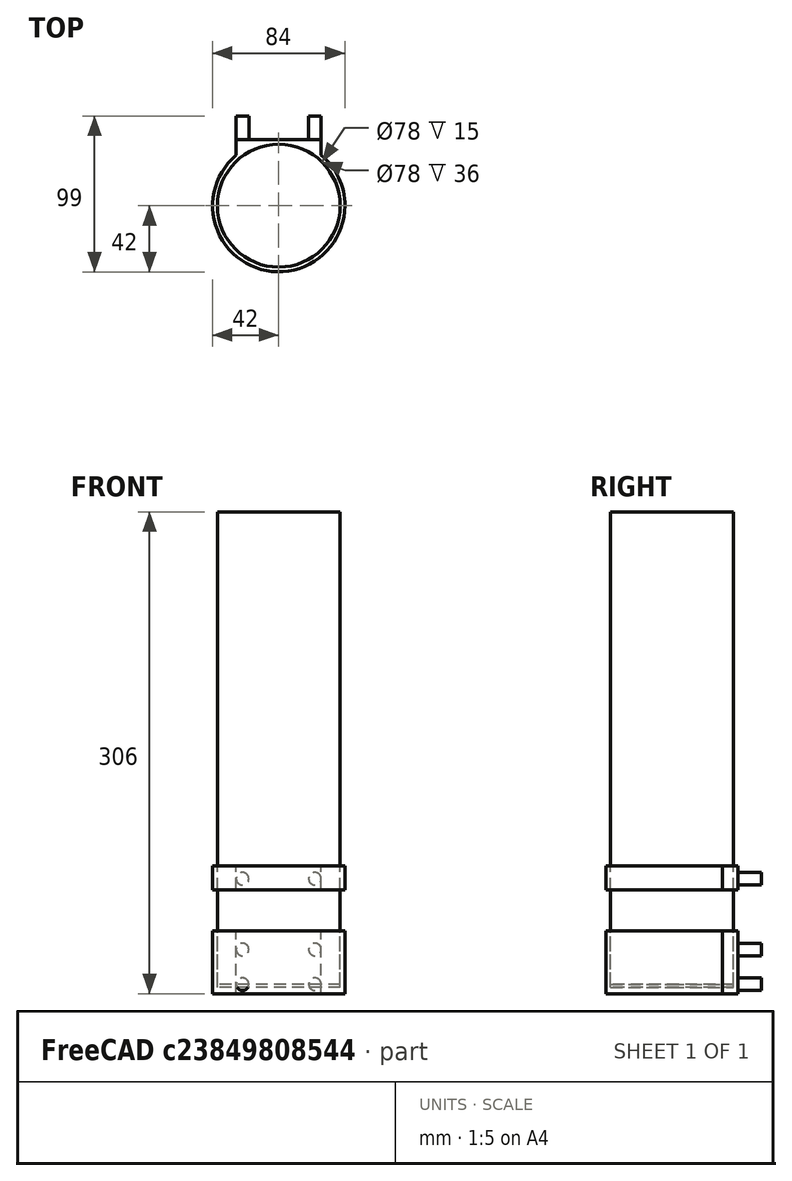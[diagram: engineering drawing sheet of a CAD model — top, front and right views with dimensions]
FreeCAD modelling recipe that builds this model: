
FCSTD DOCUMENT  (FreeCAD 0.15R4671 (Git))
Label: Holder_V10
License: All rights reserved
LicenseURL: http://en.wikipedia.org/wiki/All_rights_reserved
objects: Part::Cylinder×11, Part::Box×2, Part::MultiFuse×2, Part::Cut×2
note: 17 computed .brp shape members not serialized (recipe doc carries the construction recipe); baked Part::Feature solids carry a one-line shape summary decoded from their .brp

FEATURE [Part::Cylinder] Cylinder  label="Pin1"
  Angle = 360
  Height = 15
  Placement = pos=(0,5,0) rot=(1,0,0;1.5708rad)
  Radius = 4
FEATURE [Part::Cylinder] Cylinder001  label="Pin2"
  Angle = 360
  Height = 15
  Placement = pos=(46,5,0) rot=(1,0,0;1.5708rad)
  Radius = 4
FEATURE [Part::Cylinder] Cylinder002  label="Pin3"
  Angle = 360
  Height = 15
  Placement = pos=(0,5,22) rot=(1,0,0;1.5708rad)
  Radius = 4
FEATURE [Part::Cylinder] Cylinder003  label="Pin4"
  Angle = 360
  Height = 15
  Placement = pos=(46,5,22) rot=(1,0,0;1.5708rad)
  Radius = 4
FEATURE [Part::Cylinder] Cylinder004  label="Bottle_Base"
  Angle = 360
  Height = 40
  Placement = pos=(23,-52,-6) rot=(0,0,1;0rad)
  Radius = 42
FEATURE [Part::Box] Box  label="Peg support"
  Height = 40
  Length = 54
  Placement = pos=(-4,-20,-6) rot=(0,0,1;0rad)
  Width = 10
FEATURE [Part::Cylinder] Cylinder005  label="Bottle_cut"
  Angle = 360
  Height = 36
  Placement = pos=(23,-52,-2) rot=(0,0,1;0rad)
  Radius = 39
FEATURE [Part::Cylinder] Cylinder006  label="Bottle_Belly"
  Angle = 360
  Height = 15
  Placement = pos=(23,-52,60) rot=(0,0,1;0rad)
  Radius = 42
FEATURE [Part::Cylinder] Cylinder007  label="Pin5"
  Angle = 360
  Height = 15
  Placement = pos=(0,5,67) rot=(1,0,0;1.5708rad)
  Radius = 4
FEATURE [Part::Cylinder] Cylinder008  label="Pin6"
  Angle = 360
  Height = 15
  Placement = pos=(46,5,67) rot=(1,0,0;1.5708rad)
  Radius = 4
FEATURE [Part::Cylinder] Cylinder010  label="Bottle"
  Angle = 360
  Height = 300
  Placement = pos=(23,-52,0) rot=(0,0,1;0rad)
  Radius = 39
FEATURE [Part::Box] Box001  label="Peg support001"
  Height = 15
  Length = 54
  Placement = pos=(-4,-20,60) rot=(0,0,1;0rad)
  Width = 10
FEATURE [Part::Cylinder] Cylinder011  label="Bottle_Belly_cut"
  Angle = 360
  Height = 15
  Placement = pos=(23,-52,60) rot=(0,0,1;0rad)
  Radius = 39
FEATURE [Part::MultiFuse] Fusion
  Shapes = -> [Box001,Cylinder006]
FEATURE [Part::Cut] Cut  label="Upper_part"
  Base = -> Fusion
  Tool = -> Cylinder011
FEATURE [Part::MultiFuse] Fusion001
  Shapes = -> [Cylinder004,Box]
FEATURE [Part::Cut] Cut001  label="Lower_part"
  Base = -> Fusion001
  Tool = -> Cylinder005
